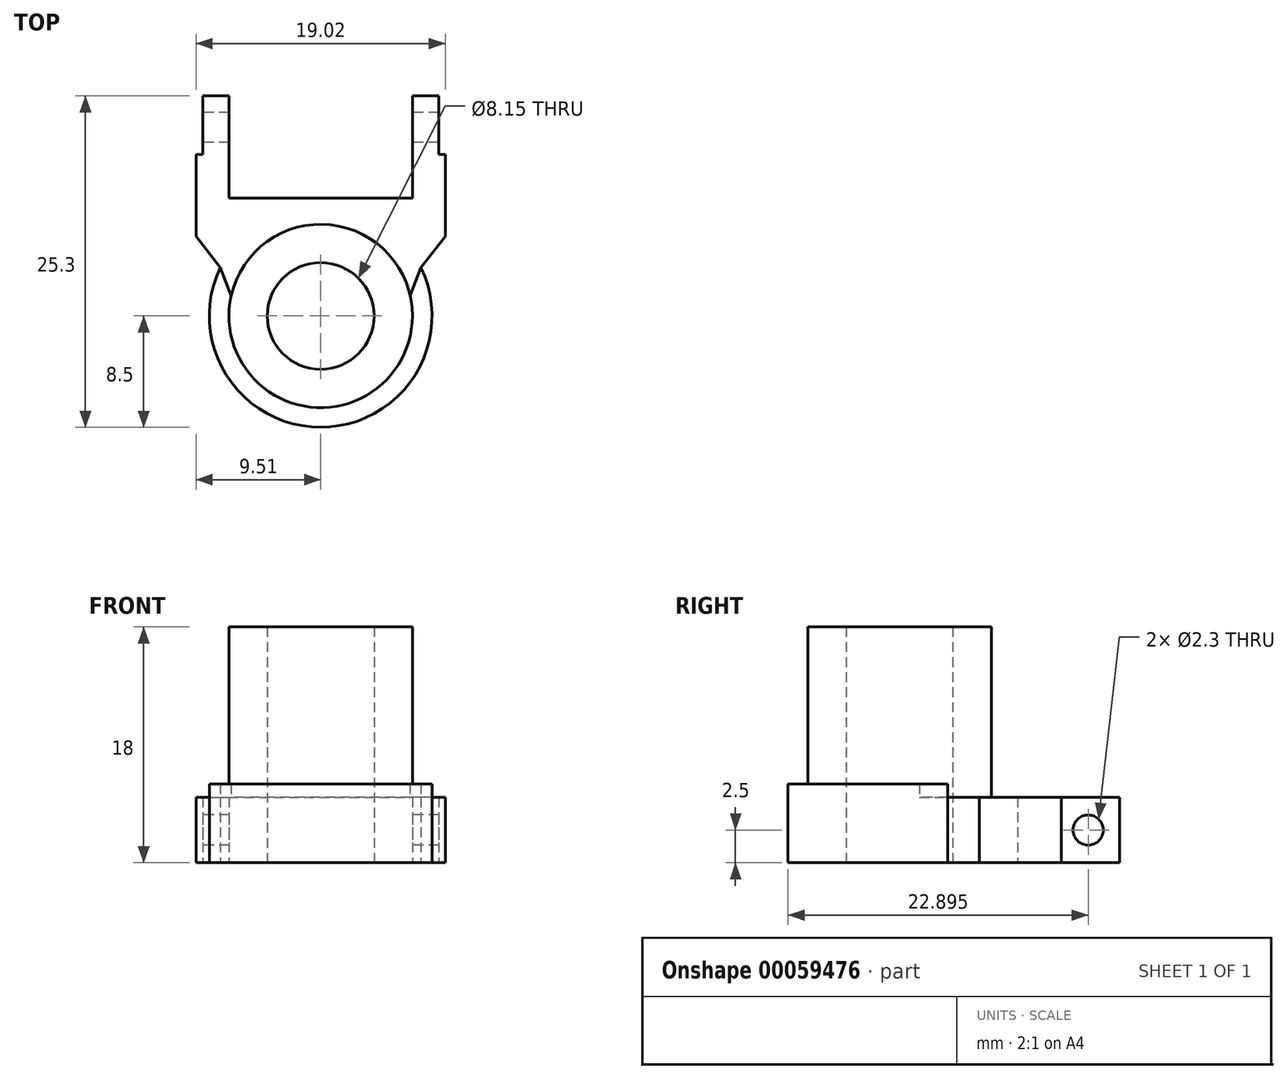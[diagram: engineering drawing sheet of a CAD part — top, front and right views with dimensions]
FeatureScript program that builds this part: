
annotation { "Feature Type Name" : "Feature", "Feature Type Description" : "" }
export const myFeature = defineFeature(function(context is Context, id is Id, definition is map)
    precondition{}
    {
        {
            var Q0;
            Q0=qCreatedBy(makeId("Top.planeOp"),FACE);
            var sketch = newSketch(context, id + "F0", { "sketchPlane" : qUnion([Q0])});
            skLineSegment(sketch, "E0", {"start": v(-65.2, 0) * mm, "end": v(71.29, 0) * mm, "construction": true});
            skLineSegment(sketch, "E1", {"start": v(0, 54.68) * mm, "end": v(0, -53.77) * mm, "construction": true});
            skLineSegment(sketch, "E2.0", {"start": v(7, 54.68) * mm, "end": v(7, -53.77) * mm, "construction": true});
            skLineSegment(sketch, "E3.0", {"start": v(-7, 54.68) * mm, "end": v(-7, -53.77) * mm, "construction": true});
            skCircle(sketch, "E4", {"center": v(0, 0) * mm, "radius": 4.08 * mm});
            skCircle(sketch, "E5", {"center": v(0, 0) * mm, "radius": 7 * mm});
            skCircle(sketch, "E6", {"center": v(0, 0) * mm, "radius": 8.5 * mm});
            skLineSegment(sketch, "E7.0", {"start": v(-65.2, 9) * mm, "end": v(71.29, 9) * mm});
            skLineSegment(sketch, "E8", {"start": v(-7, 9) * mm, "end": v(-7, 12.34) * mm});
            skLineSegment(sketch, "E9", {"start": v(-7, 12.34) * mm, "end": v(-9.51, 12.34) * mm});
            skLineSegment(sketch, "E10", {"start": v(-9.51, 12.34) * mm, "end": v(-9.51, 6.1) * mm});
            skLineSegment(sketch, "E11", {"start": v(-9.51, 6.1) * mm, "end": v(-7.66, 3.69) * mm});
            skLineSegment(sketch, "E12", {"start": v(0, 9) * mm, "end": v(0, 8.5) * mm});
            skLineSegment(sketch, "E13.MirrorCS", {"start": v(65.2, 9) * mm, "end": v(-71.29, 9) * mm});
            skLineSegment(sketch, "E14.MirrorCS", {"start": v(7, 9) * mm, "end": v(7, 12.34) * mm});
            skLineSegment(sketch, "E15.MirrorCS", {"start": v(7, 12.34) * mm, "end": v(9.51, 12.34) * mm});
            skLineSegment(sketch, "E16.MirrorCS", {"start": v(9.51, 12.34) * mm, "end": v(9.51, 6.1) * mm});
            skLineSegment(sketch, "E17.MirrorCS", {"start": v(9.51, 6.1) * mm, "end": v(7.66, 3.69) * mm});
            skLineSegment(sketch, "E18", {"start": v(-7.66, 3.69) * mm, "end": v(-6.83, 1.53) * mm});
            skLineSegment(sketch, "E19.MirrorCS", {"start": v(7.66, 3.69) * mm, "end": v(6.83, 1.53) * mm});
            skLineSegment(sketch, "E20", {"start": v(-7, 12.34) * mm, "end": v(-7, 16.8) * mm});
            skLineSegment(sketch, "E21.0", {"start": v(-9, 12.34) * mm, "end": v(-9, 16.8) * mm});
            skLineSegment(sketch, "E22", {"start": v(-9, 16.8) * mm, "end": v(-7, 16.8) * mm});
            skLineSegment(sketch, "E23.MirrorCS", {"start": v(9, 16.8) * mm, "end": v(7, 16.8) * mm});
            skLineSegment(sketch, "E24.MirrorCS", {"start": v(9, 12.34) * mm, "end": v(9, 16.8) * mm});
            skLineSegment(sketch, "E25.MirrorCS", {"start": v(-14, 54.68) * mm, "end": v(-14, -53.77) * mm, "construction": true});
            skLineSegment(sketch, "E26.MirrorCS", {"start": v(7, 12.34) * mm, "end": v(7, 16.8) * mm});
            skSolve(sketch);
        }
        {
            var Q0;
            Q0=makeQuery(id+"F0.imprint","IMPRINT",FACE,{"disambiguationData":[TD([[makeQuery(id+"F0.imprint","IMPRINT",EDGE,{"derivedFrom":sQuery(id+"F0.wireOp",EDGE,"E4")}),-1.0]])]});
            extrude(context, id + "F1", {"entities" : qUnion([Q0]), "depth" : 18 * mm});
        }
        {
            var Q0;
            {var subQ0=sQuery(id+"F0.wireOp",EDGE,"E8");Q0=makeQuery(id+"F0.imprint","IMPRINT",FACE,{"disambiguationData":[TD([[makeQuery(id+"F0.imprint","IMPRINT",EDGE,{"derivedFrom":subQ0}),1.0]])]});}
            var Q1;
            {var subQ1=sQuery(id+"F0.wireOp",EDGE,"E11");Q1=makeQuery(id+"F0.imprint","IMPRINT",FACE,{"disambiguationData":[TD([[makeQuery(id+"F0.imprint","IMPRINT",EDGE,{"derivedFrom":subQ1}),1.0]])]});}
            var Q2;
            {var subQ0=sQuery(id+"F0.wireOp",EDGE,"E18");Q2=makeQuery(id+"F0.imprint","IMPRINT",FACE,{"disambiguationData":[TD([[makeQuery(id+"F0.imprint","IMPRINT",EDGE,{"derivedFrom":subQ0}),1.0]])]});}
            var Q3;
            {var subQ1=sQuery(id+"F0.wireOp",EDGE,"E12");Q3=makeQuery(id+"F0.imprint","IMPRINT",FACE,{"disambiguationData":[TD([[makeQuery(id+"F0.imprint","IMPRINT",EDGE,{"derivedFrom":subQ1}),1.0]])]});}
            var Q4;
            {var subQ0=sQuery(id+"F0.wireOp",EDGE,"E14.MirrorCS");Q4=makeQuery(id+"F0.imprint","IMPRINT",FACE,{"disambiguationData":[TD([[makeQuery(id+"F0.imprint","IMPRINT",EDGE,{"derivedFrom":subQ0}),-1.0]])]});}
            var Q5;
            {var subQ0=sQuery(id+"F0.wireOp",EDGE,"E20");Q5=makeQuery(id+"F0.imprint","IMPRINT",FACE,{"disambiguationData":[TD([[makeQuery(id+"F0.imprint","IMPRINT",EDGE,{"derivedFrom":subQ0}),1.0]])]});}
            var Q6;
            Q6=makeQuery(id+"F0.imprint","IMPRINT",FACE,{"disambiguationData":[TD([[makeQuery(id+"F0.imprint","IMPRINT",EDGE,{"derivedFrom":sQuery(id+"F0.wireOp",EDGE,"E23.MirrorCS")}),1.0]])]});
            extrude(context, id + "F2", {"entities" : qUnion([Q0, Q1, Q2, Q3, Q4, Q5, Q6]), "operationType" : NewBodyOperationType.ADD, "depth" : 5 * mm});
        }
        {
            var Q0;
            {var subQ0=sQuery(id+"F0.wireOp",EDGE,"E18");Q0=makeQuery(id+"F0.imprint","IMPRINT",FACE,{"disambiguationData":[TD([[makeQuery(id+"F0.imprint","IMPRINT",EDGE,{"derivedFrom":subQ0}),-1.0]])]});}
            extrude(context, id + "F3", {"entities" : qUnion([Q0]), "operationType" : NewBodyOperationType.ADD, "depth" : 6 * mm});
        }
        {
            var Q0;
            Q0=makeQuery(id+"F2.opExtrude","SWEPT_FACE",FACE,{"disambiguationData":[OSD([sQuery(id+"F0.wireOp",EDGE,"E21.0")])]});
            var sketch = newSketch(context, id + "F4", { "sketchPlane" : qUnion([Q0])});
            skLineSegment(sketch, "E27.0", {"start": v(-12.34, 5) * mm, "end": v(-16.8, 5) * mm});
            skLineSegment(sketch, "E28.0", {"start": v(-12.34, 0) * mm, "end": v(-16.8, 0) * mm});
            skLineSegment(sketch, "E29.0", {"start": v(-16.8, 5) * mm, "end": v(-16.8, 0) * mm});
            skLineSegment(sketch, "E30", {"start": v(-14.57, 5) * mm, "end": v(-14.22, 0) * mm, "construction": true});
            skCircle(sketch, "E31", {"center": v(-14.4, 2.5) * mm, "radius": 1.15 * mm});
            skSolve(sketch);
        }
        {
            var Q0;
            Q0=makeQuery(id+"F4.imprint","IMPRINT",FACE,{"disambiguationData":[TD([[makeQuery(id+"F4.imprint","IMPRINT",EDGE,{"derivedFrom":sQuery(id+"F4.wireOp",EDGE,"E31")}),1.0]])]});
            var Q1;
            Q1=sQuery(id+"F4.wireOp",EDGE,"E31");
            extrude(context, id + "F5", {"entities" : qUnion([Q0]), "operationType" : NewBodyOperationType.REMOVE, "surfaceEntities" : qUnion([Q1]), "oppositeDirection" : true, "depth" : 25 * mm});
        }
    });
